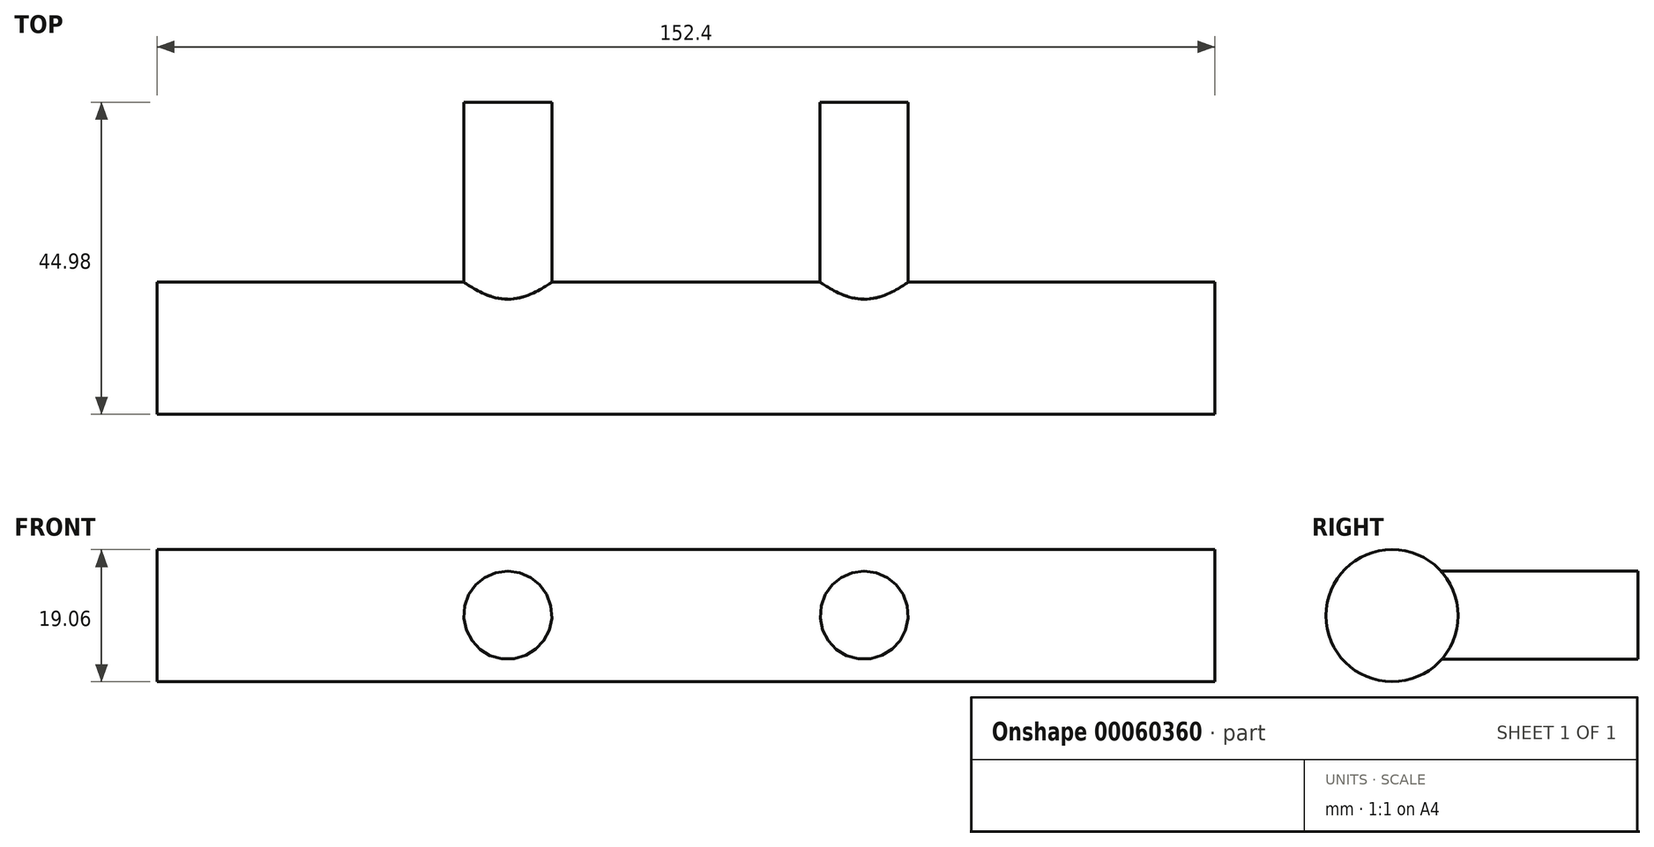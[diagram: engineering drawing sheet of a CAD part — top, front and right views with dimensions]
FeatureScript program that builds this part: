
annotation { "Feature Type Name" : "Feature", "Feature Type Description" : "" }
export const myFeature = defineFeature(function(context is Context, id is Id, definition is map)
    precondition{}
    {
        {
            var Q0;
            Q0=qCreatedBy(makeId("Front.planeOp"),FACE);
            var sketch = newSketch(context, id + "F0", { "sketchPlane" : qUnion([Q0])});
            skCircle(sketch, "E0", {"center": v(-25.67, 0.08) * mm, "radius": 6.35 * mm});
            skCircle(sketch, "E1.MirrorC", {"center": v(25.67, 0.08) * mm, "radius": 6.35 * mm});
            skSolve(sketch);
        }
        {
            var Q0;
            Q0=qCreatedBy(makeId("Right.planeOp"),FACE);
            var sketch = newSketch(context, id + "F1", { "sketchPlane" : qUnion([Q0])});
            skCircle(sketch, "E2", {"center": v(-35.45, 0) * mm, "radius": 9.53 * mm});
            skSolve(sketch);
        }
        {
            var Q0;
            Q0=makeQuery(id+"F1.imprint","IMPRINT",FACE,{"disambiguationData":[TD([[makeQuery(id+"F1.imprint","IMPRINT",EDGE,{"derivedFrom":sQuery(id+"F1.wireOp",EDGE,"E2")}),1.0]])]});
            extrude(context, id + "F2", {"entities" : qUnion([Q0]), "endBound" : BoundingType.SYMMETRIC, "depth" : 152.4 * mm});
        }
        {
            var Q0;
            Q0 = qSketchRegion(id + "F0", true);
            extrude(context, id + "F3", {"entities" : qUnion([Q0]), "operationType" : NewBodyOperationType.ADD, "depth" : 32.38 * mm});
        }
    });
